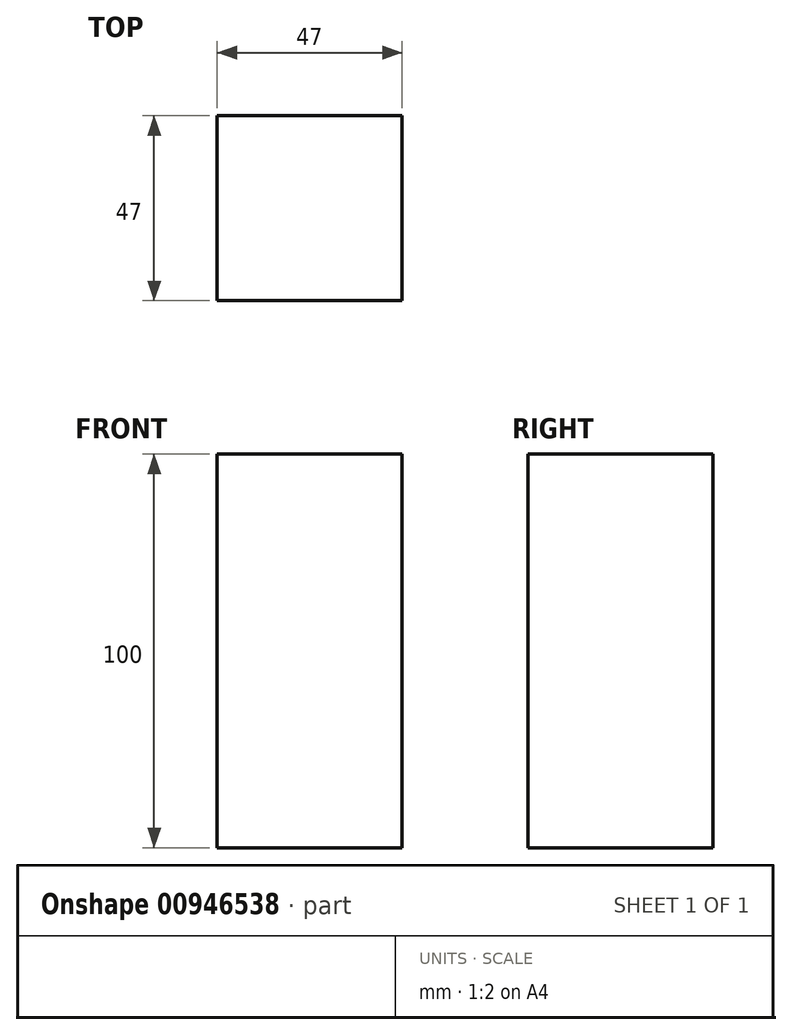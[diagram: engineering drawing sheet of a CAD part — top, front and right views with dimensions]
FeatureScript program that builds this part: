
annotation { "Feature Type Name" : "Feature", "Feature Type Description" : "" }
export const myFeature = defineFeature(function(context is Context, id is Id, definition is map)
    precondition{}
    {
        {
            var Q0;
            Q0=qCreatedBy(makeId("Top.planeOp"),FACE);
            var sketch = newSketch(context, id + "F0", { "sketchPlane" : qUnion([Q0])});
            skLineSegment(sketch, "E0.bottom", {"start": v(23.5, -23.5) * mm, "end": v(-23.5, -23.5) * mm});
            skLineSegment(sketch, "E0.top", {"start": v(23.5, 23.5) * mm, "end": v(-23.5, 23.5) * mm});
            skLineSegment(sketch, "E0.left", {"start": v(23.5, -23.5) * mm, "end": v(23.5, 23.5) * mm});
            skLineSegment(sketch, "E0.right", {"start": v(-23.5, -23.5) * mm, "end": v(-23.5, 23.5) * mm});
            skPoint(sketch, "E0.middle", {"position": v(0, 0) * mm});
            skSolve(sketch);
        }
        {
            var Q0;
            Q0 = qSketchRegion(id + "F0", true);
            extrude(context, id + "F1", {"entities" : qUnion([Q0]), "oppositeDirection" : true, "depth" : 100 * mm, "offsetDistance" : 25 * mm});
        }
    });
